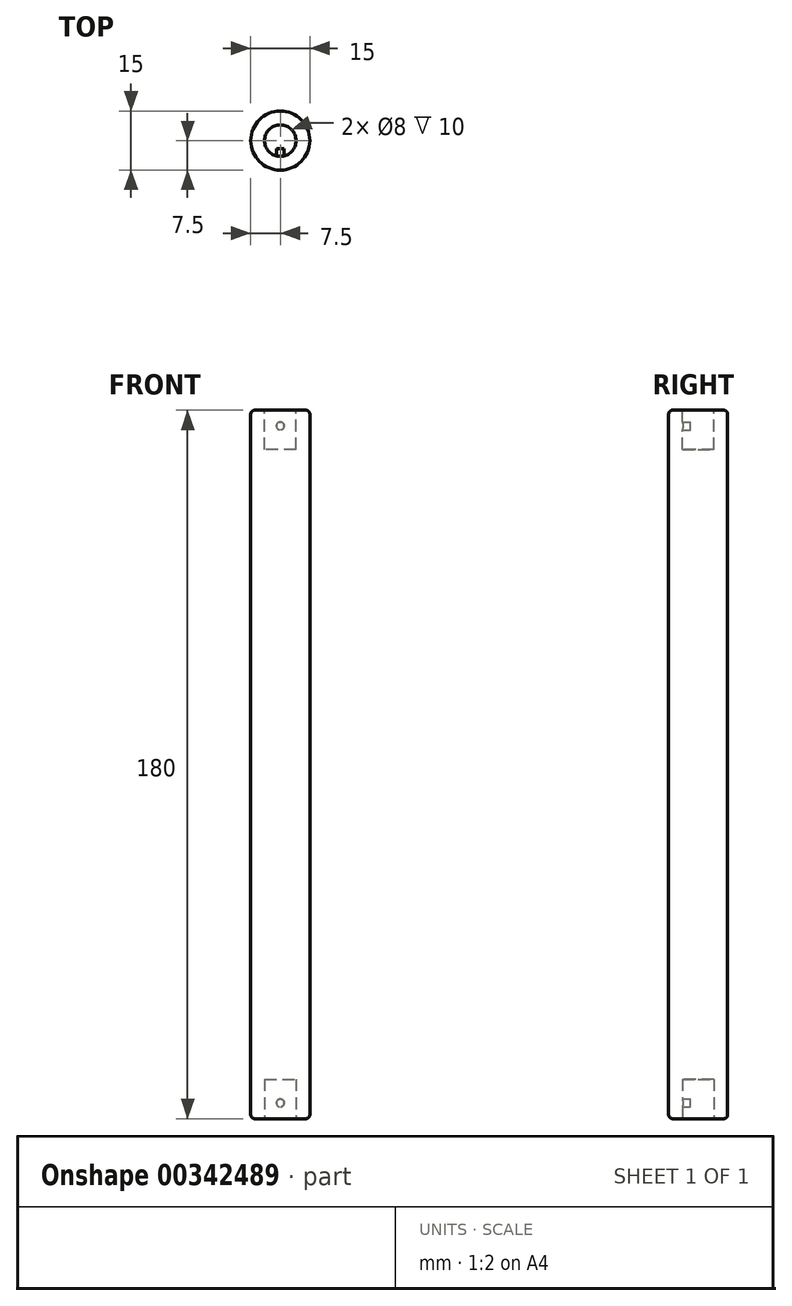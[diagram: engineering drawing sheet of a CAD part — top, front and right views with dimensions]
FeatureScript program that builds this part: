
annotation { "Feature Type Name" : "Feature", "Feature Type Description" : "" }
export const myFeature = defineFeature(function(context is Context, id is Id, definition is map)
    precondition{}
    {
        {
            var Q0;
            Q0=qCreatedBy(makeId("Top.planeOp"),FACE);
            var sketch = newSketch(context, id + "F0", { "sketchPlane" : qUnion([Q0])});
            skCircle(sketch, "E0", {"center": v(0, 0) * mm, "radius": 7.5 * mm});
            skSolve(sketch);
        }
        {
            var Q0;
            Q0=makeQuery(id+"F0.imprint","IMPRINT",FACE,{"disambiguationData":[TD([[makeQuery(id+"F0.imprint","IMPRINT",EDGE,{"derivedFrom":sQuery(id+"F0.wireOp",EDGE,"E0")}),1.0]])]});
            extrude(context, id + "F1", {"entities" : qUnion([Q0]), "endBound" : BoundingType.SYMMETRIC, "depth" : 180 * mm});
        }
        {
            var Q0;
            Q0=makeQuery(id+"F1.opExtrude","CAP_FACE",FACE,{"disambiguationData":[OSD([sQuery(id+"F0.wireOp",EDGE,"E0")])],"isStart":false});
            var sketch = newSketch(context, id + "F2", { "sketchPlane" : qUnion([Q0])});
            skCircle(sketch, "E1", {"center": v(0, 0) * mm, "radius": 4 * mm});
            skSolve(sketch);
        }
        {
            var Q0;
            Q0=makeQuery(id+"F2.imprint","IMPRINT",FACE,{"disambiguationData":[TD([[makeQuery(id+"F2.imprint","IMPRINT",EDGE,{"derivedFrom":sQuery(id+"F2.wireOp",EDGE,"E1")}),1.0]])]});
            extrude(context, id + "F3", {"entities" : qUnion([Q0]), "operationType" : NewBodyOperationType.REMOVE, "oppositeDirection" : true, "depth" : 10 * mm});
        }
        {
            var Q0;
            Q0=makeQuery(id+"F1.opExtrude","CAP_FACE",FACE,{"disambiguationData":[OSD([sQuery(id+"F0.wireOp",EDGE,"E0")])],"isStart":true});
            var sketch = newSketch(context, id + "F4", { "sketchPlane" : qUnion([Q0])});
            skCircle(sketch, "E2", {"center": v(0, 0) * mm, "radius": 4 * mm});
            skSolve(sketch);
        }
        {
            var Q0;
            Q0=makeQuery(id+"F4.imprint","IMPRINT",FACE,{"disambiguationData":[TD([[makeQuery(id+"F4.imprint","IMPRINT",EDGE,{"derivedFrom":sQuery(id+"F4.wireOp",EDGE,"E2")}),1.0]])]});
            extrude(context, id + "F5", {"entities" : qUnion([Q0]), "operationType" : NewBodyOperationType.REMOVE, "oppositeDirection" : true, "depth" : 10 * mm});
        }
        {
            var Q0;
            Q0=qCreatedBy(makeId("Front.planeOp"),FACE);
            var sketch = newSketch(context, id + "F6", { "sketchPlane" : qUnion([Q0])});
            skCircle(sketch, "E3", {"center": v(0, 86) * mm, "radius": 1 * mm});
            skCircle(sketch, "E4", {"center": v(0, -86) * mm, "radius": 1 * mm});
            skSolve(sketch);
        }
        {
            var Q0;
            Q0=makeQuery(id+"F6.imprint","IMPRINT",FACE,{"disambiguationData":[TD([[makeQuery(id+"F6.imprint","IMPRINT",EDGE,{"derivedFrom":sQuery(id+"F6.wireOp",EDGE,"E3")}),1.0]])]});
            var Q1;
            Q1=makeQuery(id+"F6.imprint","IMPRINT",FACE,{"disambiguationData":[TD([[makeQuery(id+"F6.imprint","IMPRINT",EDGE,{"derivedFrom":sQuery(id+"F6.wireOp",EDGE,"E4")}),1.0]])]});
            var Q2;
            Q2=makeQuery(id+"F3.boolean.opBoolean","COPY",FACE,{"derivedFrom":makeQuery(id+"F3.opExtrude","SWEPT_FACE",FACE,{"disambiguationData":[OSD([sQuery(id+"F2.wireOp",EDGE,"E1")])]})});
            extrude(context, id + "F7", {"entities" : qUnion([Q0, Q1]), "operationType" : NewBodyOperationType.ADD, "endBound" : BoundingType.UP_TO_SURFACE, "endBoundEntityFace" : qUnion([Q2]), "depth" : 25 * mm});
        }
        {
            var Q0;
            Q0=makeQuery(id+"F7.opExtrude","CAP_FACE",FACE,{"disambiguationData":[OSD([sQuery(id+"F6.wireOp",EDGE,"E3")])],"isStart":true});
            var Q1;
            Q1=makeQuery(id+"F7.opExtrude","CAP_FACE",FACE,{"disambiguationData":[OSD([sQuery(id+"F6.wireOp",EDGE,"E4")])],"isStart":true});
            extrude(context, id + "F8", {"entities" : qUnion([Q0, Q1]), "operationType" : NewBodyOperationType.REMOVE, "oppositeDirection" : true, "depth" : 2 * mm});
        }
        {
            var Q0;
            Q0=makeQuery(id+"F1.opExtrude","CAP_EDGE",EDGE,{"disambiguationData":[OSD([sQuery(id+"F0.wireOp",EDGE,"E0")])],"isStart":true});
            var Q1;
            Q1=makeQuery(id+"F5.boolean.opBoolean","COPY",EDGE,{"derivedFrom":makeQuery(id+"F5.opExtrude","CAP_EDGE",EDGE,{"disambiguationData":[OSD([sQuery(id+"F4.wireOp",EDGE,"E2")])],"isStart":true})});
            var Q2;
            Q2=makeQuery(id+"F1.opExtrude","CAP_EDGE",EDGE,{"disambiguationData":[OSD([sQuery(id+"F0.wireOp",EDGE,"E0")])],"isStart":false});
            var Q3;
            Q3=makeQuery(id+"F3.boolean.opBoolean","COPY",EDGE,{"derivedFrom":makeQuery(id+"F3.opExtrude","CAP_EDGE",EDGE,{"disambiguationData":[OSD([sQuery(id+"F2.wireOp",EDGE,"E1")])],"isStart":true})});
            fillet(context, id + "F9", {"entities" : qUnion([Q0, Q1, Q2, Q3]), "radius" : 1 * mm, "tangentPropagation" : true, "allowEdgeOverflow" : false});
        }
    });
